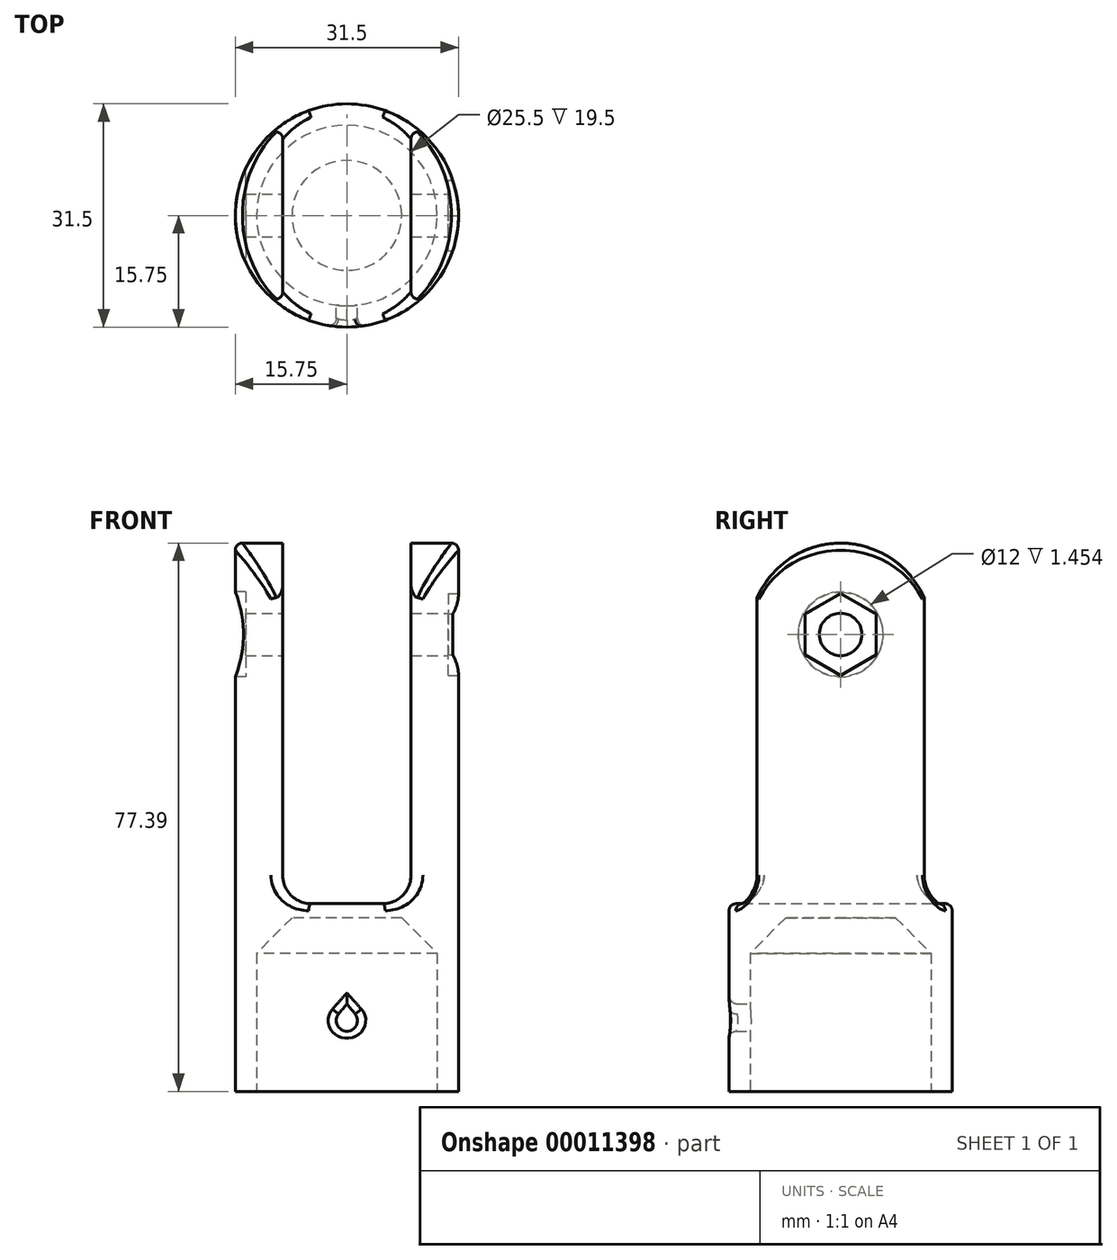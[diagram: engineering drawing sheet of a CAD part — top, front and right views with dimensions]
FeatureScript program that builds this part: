
annotation { "Feature Type Name" : "Feature", "Feature Type Description" : "" }
export const myFeature = defineFeature(function(context is Context, id is Id, definition is map)
    precondition{}
    {
        {
            var Q0;
            Q0=qCreatedBy(makeId("Top.planeOp"),FACE);
            var sketch = newSketch(context, id + "F0", { "sketchPlane" : qUnion([Q0])});
            skCircle(sketch, "E0", {"center": v(0, 0) * mm, "radius": 12.75 * mm});
            skCircle(sketch, "E1", {"center": v(0, 0) * mm, "radius": 15.75 * mm});
            skSolve(sketch);
        }
        {
            var Q0;
            Q0 = qSketchRegion(id + "F0", true);
            extrude(context, id + "F1", {"entities" : qUnion([Q0]), "depth" : 25 * mm});
        }
        {
            var Q0;
            Q0=qCreatedBy(makeId("Front.planeOp"),FACE);
            var sketch = newSketch(context, id + "F2", { "sketchPlane" : qUnion([Q0])});
            skLineSegment(sketch, "E2.bottom", {"start": v(-7.4, 101) * mm, "end": v(7.4, 101) * mm, "construction": true});
            skLineSegment(sketch, "E2.top", {"start": v(-7.4, 28) * mm, "end": v(7.4, 28) * mm, "construction": true});
            skLineSegment(sketch, "E2.left", {"start": v(-7.4, 101) * mm, "end": v(-7.4, 28) * mm, "construction": true});
            skLineSegment(sketch, "E2.right", {"start": v(7.4, 101) * mm, "end": v(7.4, 28) * mm, "construction": true});
            skLineSegment(sketch, "E3", {"start": v(7.4, 64.5) * mm, "end": v(-7.4, 64.5) * mm, "construction": true});
            skSolve(sketch);
        }
        {
            var Q0;
            Q0=makeQuery(id+"F1.opExtrude","CAP_FACE",FACE,{"disambiguationData":[OSD([sQuery(id+"F0.wireOp",EDGE,"E0"),sQuery(id+"F0.wireOp",EDGE,"E1")])],"isStart":false});
            var sketch = newSketch(context, id + "F3", { "sketchPlane" : qUnion([Q0])});
            skLineSegment(sketch, "E4", {"start": v(-9.05, 12.9) * mm, "end": v(-9.05, -12.9) * mm});
            skLineSegment(sketch, "E5", {"start": v(9.05, 12.9) * mm, "end": v(9.05, -12.9) * mm});
            skArc(sketch, "E6", {"start": v(-9.05, 12.9) * mm, "mid": v(-15.75, 0) * mm, "end": v(-9.05, -12.9) * mm});
            skArc(sketch, "E7", {"start": v(-9.05, 8.98) * mm, "mid": v(-12.75, 0) * mm, "end": v(-9.05, -8.98) * mm});
            skArc(sketch, "E8.trimOffspring", {"start": v(9.05, -8.98) * mm, "mid": v(12.75, 0) * mm, "end": v(9.05, 8.98) * mm});
            skArc(sketch, "E9.trimOffspring", {"start": v(9.05, -12.9) * mm, "mid": v(15.75, 0) * mm, "end": v(9.05, 12.9) * mm});
            skSolve(sketch);
        }
        {
            var Q0;
            Q0 = qSketchRegion(id + "F3", true);
            extrude(context, id + "F4", {"entities" : qUnion([Q0]), "operationType" : NewBodyOperationType.ADD, "depth" : 60 * mm});
        }
        {
            var Q0;
            Q0=qCreatedBy(makeId("Right.planeOp"),FACE);
            var sketch = newSketch(context, id + "F5", { "sketchPlane" : qUnion([Q0])});
            skArc(sketch, "E10", {"start": v(-12.9, 64.5) * mm, "mid": v(0, 77.4) * mm, "end": v(12.9, 64.5) * mm});
            skLineSegment(sketch, "E11", {"start": v(-12.9, 64.5) * mm, "end": v(-23.57, 86.22) * mm});
            skLineSegment(sketch, "E12", {"start": v(-23.57, 86.22) * mm, "end": v(28.46, 88.54) * mm});
            skLineSegment(sketch, "E13", {"start": v(28.46, 88.54) * mm, "end": v(12.9, 64.5) * mm});
            skCircle(sketch, "E14", {"center": v(0, 64.5) * mm, "radius": 3 * mm});
            skSolve(sketch);
        }
        {
            var Q0;
            Q0 = qSketchRegion(id + "F5", true);
            extrude(context, id + "F6", {"entities" : qUnion([Q0]), "operationType" : NewBodyOperationType.REMOVE, "oppositeDirection" : true, "depth" : 50 * mm, "hasSecondDirection" : true, "secondDirectionOppositeDirection" : false, "secondDirectionDepth" : 50 * mm});
        }
        {
            var Q0;
            Q0=qCreatedBy(makeId("Front.planeOp"),FACE);
            var sketch = newSketch(context, id + "F7", { "sketchPlane" : qUnion([Q0])});
            skLineSegment(sketch, "E15", {"start": v(-1.15, 10.96) * mm, "end": v(0, 12.33) * mm});
            skLineSegment(sketch, "E16", {"start": v(0, 12.33) * mm, "end": v(1.15, 10.96) * mm});
            skArc(sketch, "E17", {"start": v(-1.15, 10.96) * mm, "mid": v(0, 8.5) * mm, "end": v(1.15, 10.96) * mm});
            skSolve(sketch);
        }
        {
            var Q0;
            Q0 = qSketchRegion(id + "F7", true);
            extrude(context, id + "F8", {"entities" : qUnion([Q0]), "operationType" : NewBodyOperationType.REMOVE, "endBound" : BoundingType.THROUGH_ALL, "depth" : 25 * mm});
        }
        {
            var Q0;
            Q0=qCreatedBy(makeId("Right.planeOp"),FACE);
            cPlane(context, id + "F9", {"entities" : qUnion([Q0]), "cplaneType" : CPlaneType.OFFSET, "offset" : 50 * mm, "width" : 150 * mm, "height" : 150 * mm});
        }
        {
            var Q0;
            Q0=qCreatedBy(id+"F9.planeOp",FACE);
            var sketch = newSketch(context, id + "F10", { "sketchPlane" : qUnion([Q0])});
            skCircle(sketch, "E18.cCircle", {"center": v(0, 64.5) * mm, "radius": 5.77 * mm, "construction": true});
            skLineSegment(sketch, "E18.0", {"start": v(5, 67.39) * mm, "end": v(5, 61.61) * mm});
            skLineSegment(sketch, "E18.1", {"start": v(5, 61.61) * mm, "end": v(0, 58.73) * mm});
            skLineSegment(sketch, "E18.2", {"start": v(0, 58.73) * mm, "end": v(-5, 61.61) * mm});
            skLineSegment(sketch, "E18.3", {"start": v(-5, 61.61) * mm, "end": v(-5, 67.39) * mm});
            skLineSegment(sketch, "E18.4", {"start": v(-5, 67.39) * mm, "end": v(0, 70.27) * mm});
            skLineSegment(sketch, "E18.5", {"start": v(0, 70.27) * mm, "end": v(5, 67.39) * mm});
            skSolve(sketch);
        }
        {
            var Q0;
            Q0 = qSketchRegion(id + "F10", true);
            var Q1;
            Q1=makeQuery(id+"F4.boolean.opBoolean","MERGE",FACE,{"derivedFrom":[makeQuery(id+"F1.opExtrude","SWEPT_FACE",FACE,{"disambiguationData":[OSD([sQuery(id+"F0.wireOp",EDGE,"E1")])]}),makeQuery(id+"F4.opExtrude","SWEPT_FACE",FACE,{"disambiguationData":[OSD([sQuery(id+"F3.wireOp",EDGE,"E6")])]}),makeQuery(id+"F4.opExtrude","SWEPT_FACE",FACE,{"disambiguationData":[OSD([sQuery(id+"F3.wireOp",EDGE,"E9.trimOffspring")])]})]});
            extrude(context, id + "F11", {"entities" : qUnion([Q0]), "operationType" : NewBodyOperationType.REMOVE, "oppositeDirection" : true, "endBoundEntityFace" : qUnion([Q1]), "depth" : 35.7 * mm});
        }
        {
            var Q0;
            Q0=qCreatedBy(makeId("Right.planeOp"),FACE);
            cPlane(context, id + "F12", {"entities" : qUnion([Q0]), "cplaneType" : CPlaneType.OFFSET, "offset" : 25 * mm, "oppositeDirection" : true, "width" : 150 * mm, "height" : 150 * mm});
        }
        {
            var Q0;
            Q0=qCreatedBy(id+"F12.planeOp",FACE);
            var sketch = newSketch(context, id + "F13", { "sketchPlane" : qUnion([Q0])});
            skCircle(sketch, "E19", {"center": v(0, 64.5) * mm, "radius": 6 * mm});
            skSolve(sketch);
        }
        {
            var Q0;
            Q0 = qSketchRegion(id + "F13", true);
            extrude(context, id + "F14", {"entities" : qUnion([Q0]), "operationType" : NewBodyOperationType.REMOVE, "depth" : 10.7 * mm});
        }
        {
            var Q0;
            Q0=qCreatedBy(makeId("Front.planeOp"),FACE);
            var sketch = newSketch(context, id + "F15", { "sketchPlane" : qUnion([Q0])});
            skLineSegment(sketch, "E20", {"start": v(-9.05, 30.5) * mm, "end": v(-14.86, 30.5) * mm});
            skLineSegment(sketch, "E21", {"start": v(-14.86, 30.5) * mm, "end": v(-14.86, 24.5) * mm});
            skLineSegment(sketch, "E22", {"start": v(-14.86, 24.5) * mm, "end": v(15.42, 24.5) * mm});
            skArc(sketch, "E23", {"start": v(-9.05, 30.5) * mm, "mid": v(-7.88, 27.67) * mm, "end": v(-5.05, 26.5) * mm});
            skLineSegment(sketch, "E24", {"start": v(-5.05, 26.5) * mm, "end": v(5.05, 26.5) * mm});
            skArc(sketch, "E25", {"start": v(5.05, 26.5) * mm, "mid": v(7.88, 27.67) * mm, "end": v(9.05, 30.5) * mm});
            skLineSegment(sketch, "E26", {"start": v(9.05, 30.5) * mm, "end": v(15.42, 30.5) * mm});
            skLineSegment(sketch, "E27", {"start": v(15.42, 30.5) * mm, "end": v(15.42, 24.5) * mm});
            skSolve(sketch);
        }
        {
            var Q0;
            Q0 = qSketchRegion(id + "F15", true);
            var Q1;
            Q1=makeQuery(id+"F4.boolean.opBoolean","MERGE",FACE,{"derivedFrom":[makeQuery(id+"F1.opExtrude","SWEPT_FACE",FACE,{"disambiguationData":[OSD([sQuery(id+"F0.wireOp",EDGE,"E1")])]}),makeQuery(id+"F4.opExtrude","SWEPT_FACE",FACE,{"disambiguationData":[OSD([sQuery(id+"F3.wireOp",EDGE,"E6")])]}),makeQuery(id+"F4.opExtrude","SWEPT_FACE",FACE,{"disambiguationData":[OSD([sQuery(id+"F3.wireOp",EDGE,"E9.trimOffspring")])]})]});
            var Q2;
            Q2=makeQuery(id+"F4.boolean.opBoolean","MERGE",FACE,{"derivedFrom":[makeQuery(id+"F1.opExtrude","SWEPT_FACE",FACE,{"disambiguationData":[OSD([sQuery(id+"F0.wireOp",EDGE,"E1")])]}),makeQuery(id+"F4.opExtrude","SWEPT_FACE",FACE,{"disambiguationData":[OSD([sQuery(id+"F3.wireOp",EDGE,"E6")])]}),makeQuery(id+"F4.opExtrude","SWEPT_FACE",FACE,{"disambiguationData":[OSD([sQuery(id+"F3.wireOp",EDGE,"E9.trimOffspring")])]})]});
            extrude(context, id + "F16", {"entities" : qUnion([Q0]), "operationType" : NewBodyOperationType.ADD, "endBound" : BoundingType.UP_TO_SURFACE, "endBoundEntityFace" : qUnion([Q1]), "depth" : 25 * mm, "hasSecondDirection" : true, "secondDirectionBound" : BoundingType.UP_TO_SURFACE, "secondDirectionOppositeDirection" : true, "secondDirectionBoundEntityFace" : qUnion([Q2]), "secondDirectionDepth" : 25 * mm});
        }
        {
            var Q0;
            Q0=makeQuery(id+"F16.boolean.opBoolean","INTERSECT",EDGE,{"derivedFrom":[makeQuery(id+"F1.opExtrude","SWEPT_FACE",FACE,{"disambiguationData":[OSD([sQuery(id+"F0.wireOp",EDGE,"E0")])]}),makeQuery(id+"F16.opExtrude","SWEPT_FACE",FACE,{"disambiguationData":[OSD([sQuery(id+"F15.wireOp",EDGE,"E22")])]})]});
            chamfer(context, id + "F17", {"entities" : qUnion([Q0]), "width" : 5 * mm, "tangentPropagation" : true});
        }
        {
            var Q0;
            {var subQ0=sQuery(id+"F3.wireOp",EDGE,"E6");var subQ1=sQuery(id+"F3.wireOp",EDGE,"E4");var subQ2=sQuery(id+"F0.wireOp",EDGE,"E1");Q0=makeQuery(id+"F4.opExtrude","SWEPT_EDGE",EDGE,{"disambiguationData":[OSD([subQ2,subQ1,subQ0]),TDD([makeQuery(id+"F3.imprint","INTERSECT",VERTEX,{"disambiguationData":[OD(1.0)],"derivedFrom":[makeQuery(id+"F1.opExtrude","CAP_EDGE",EDGE,{"disambiguationData":[OSD([subQ2])],"isStart":false}),subQ1,subQ0]})])]});}
            var Q1;
            {var subQ0=sQuery(id+"F3.wireOp",EDGE,"E9.trimOffspring");var subQ1=sQuery(id+"F3.wireOp",EDGE,"E5");var subQ2=sQuery(id+"F0.wireOp",EDGE,"E1");Q1=makeQuery(id+"F4.opExtrude","SWEPT_EDGE",EDGE,{"disambiguationData":[OSD([subQ2,subQ1,subQ0]),TDD([makeQuery(id+"F3.imprint","INTERSECT",VERTEX,{"disambiguationData":[OD(0.0)],"derivedFrom":[makeQuery(id+"F1.opExtrude","CAP_EDGE",EDGE,{"disambiguationData":[OSD([subQ2])],"isStart":false}),subQ1,subQ0]})])]});}
            var Q2;
            Q2=makeQuery(id+"F6.boolean.opBoolean","INTERSECT",EDGE,{"disambiguationData":[OD(1.0)],"derivedFrom":[makeQuery(id+"F4.boolean.opBoolean","MERGE",FACE,{"derivedFrom":[makeQuery(id+"F1.opExtrude","SWEPT_FACE",FACE,{"disambiguationData":[OSD([sQuery(id+"F0.wireOp",EDGE,"E1")])]}),makeQuery(id+"F4.opExtrude","SWEPT_FACE",FACE,{"disambiguationData":[OSD([sQuery(id+"F3.wireOp",EDGE,"E6")])]}),makeQuery(id+"F4.opExtrude","SWEPT_FACE",FACE,{"disambiguationData":[OSD([sQuery(id+"F3.wireOp",EDGE,"E9.trimOffspring")])]})]}),makeQuery(id+"F6.opExtrude","SWEPT_FACE",FACE,{"disambiguationData":[OSD([sQuery(id+"F5.wireOp",EDGE,"E10")])]})]});
            var Q3;
            Q3=makeQuery(id+"F6.boolean.opBoolean","INTERSECT",EDGE,{"disambiguationData":[OD(0.0)],"derivedFrom":[makeQuery(id+"F4.boolean.opBoolean","MERGE",FACE,{"derivedFrom":[makeQuery(id+"F1.opExtrude","SWEPT_FACE",FACE,{"disambiguationData":[OSD([sQuery(id+"F0.wireOp",EDGE,"E1")])]}),makeQuery(id+"F4.opExtrude","SWEPT_FACE",FACE,{"disambiguationData":[OSD([sQuery(id+"F3.wireOp",EDGE,"E6")])]}),makeQuery(id+"F4.opExtrude","SWEPT_FACE",FACE,{"disambiguationData":[OSD([sQuery(id+"F3.wireOp",EDGE,"E9.trimOffspring")])]})]}),makeQuery(id+"F6.opExtrude","SWEPT_FACE",FACE,{"disambiguationData":[OSD([sQuery(id+"F5.wireOp",EDGE,"E10")])]})]});
            var Q4;
            Q4=makeQuery(id+"F8.boolean.opBoolean","INTERSECT",EDGE,{"derivedFrom":[makeQuery(id+"F4.boolean.opBoolean","MERGE",FACE,{"derivedFrom":[makeQuery(id+"F1.opExtrude","SWEPT_FACE",FACE,{"disambiguationData":[OSD([sQuery(id+"F0.wireOp",EDGE,"E1")])]}),makeQuery(id+"F4.opExtrude","SWEPT_FACE",FACE,{"disambiguationData":[OSD([sQuery(id+"F3.wireOp",EDGE,"E6")])]}),makeQuery(id+"F4.opExtrude","SWEPT_FACE",FACE,{"disambiguationData":[OSD([sQuery(id+"F3.wireOp",EDGE,"E9.trimOffspring")])]})]}),makeQuery(id+"F8.opExtrude","SWEPT_FACE",FACE,{"disambiguationData":[OSD([sQuery(id+"F7.wireOp",EDGE,"E17")])]})]});
            fillet(context, id + "F18", {"entities" : qUnion([Q0, Q1, Q2, Q3, Q4]), "radius" : 1 * mm, "tangentPropagation" : true, "allowEdgeOverflow" : false});
        }
    });
